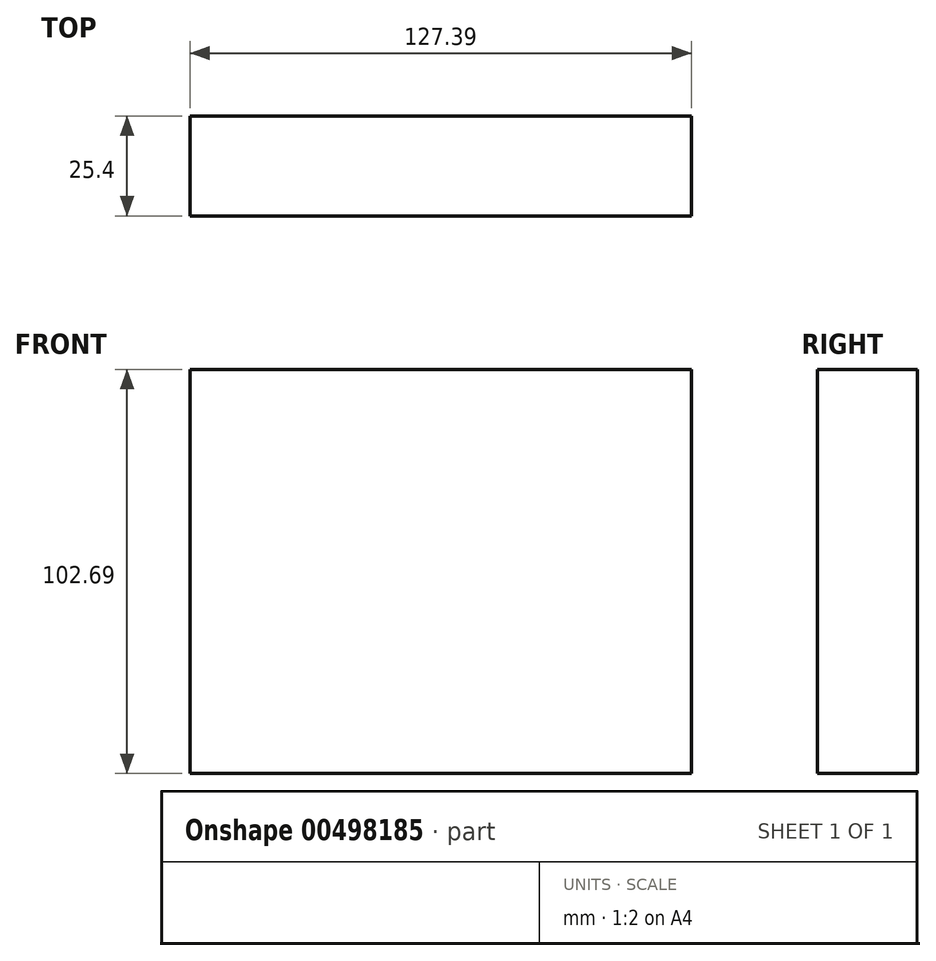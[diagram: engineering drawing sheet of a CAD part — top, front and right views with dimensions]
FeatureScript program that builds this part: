
annotation { "Feature Type Name" : "Feature", "Feature Type Description" : "" }
export const myFeature = defineFeature(function(context is Context, id is Id, definition is map)
    precondition{}
    {
        {
            var Q0;
            Q0=qCreatedBy(makeId("Front.planeOp"),FACE);
            var sketch = newSketch(context, id + "F0", { "sketchPlane" : qUnion([Q0])});
            skLineSegment(sketch, "E0.bottom", {"start": v(-70.42, 55.3) * mm, "end": v(56.97, 55.3) * mm});
            skLineSegment(sketch, "E0.top", {"start": v(-70.42, -47.38) * mm, "end": v(56.97, -47.38) * mm});
            skLineSegment(sketch, "E0.left", {"start": v(-70.42, 55.3) * mm, "end": v(-70.42, -47.38) * mm});
            skLineSegment(sketch, "E0.right", {"start": v(56.97, 55.3) * mm, "end": v(56.97, -47.38) * mm});
            skSolve(sketch);
        }
        {
            var Q0;
            Q0=makeQuery(id+"F0.imprint","IMPRINT",FACE,{"disambiguationData":[TD([[makeQuery(id+"F0.imprint","IMPRINT",EDGE,{"derivedFrom":sQuery(id+"F0.wireOp",EDGE,"E0.bottom")}),-1.0]])]});
            extrude(context, id + "F1", {"entities" : qUnion([Q0]), "depth" : 25.4 * mm});
        }
        {
            var Q0;
            Q0=makeQuery(id+"F1.opExtrude","CAP_FACE",FACE,{"disambiguationData":[OSD([sQuery(id+"F0.wireOp",EDGE,"E0.bottom"),sQuery(id+"F0.wireOp",EDGE,"E0.top"),sQuery(id+"F0.wireOp",EDGE,"E0.left"),sQuery(id+"F0.wireOp",EDGE,"E0.right")])],"isStart":true});
            var sketch = newSketch(context, id + "F2", { "sketchPlane" : qUnion([Q0])});
            skCircle(sketch, "E1", {"center": v(-30.75, 37.3) * mm, "radius": 6.9 * mm});
            skSolve(sketch);
        }
        {
            var Q0;
            Q0=sQuery(id+"F2.wireOp",EDGE,"E1");
            extrude(context, id + "F3", {"bodyType" : ToolBodyType.SURFACE, "surfaceEntities" : qUnion([Q0]), "depth" : 25.4 * mm});
        }
    });
